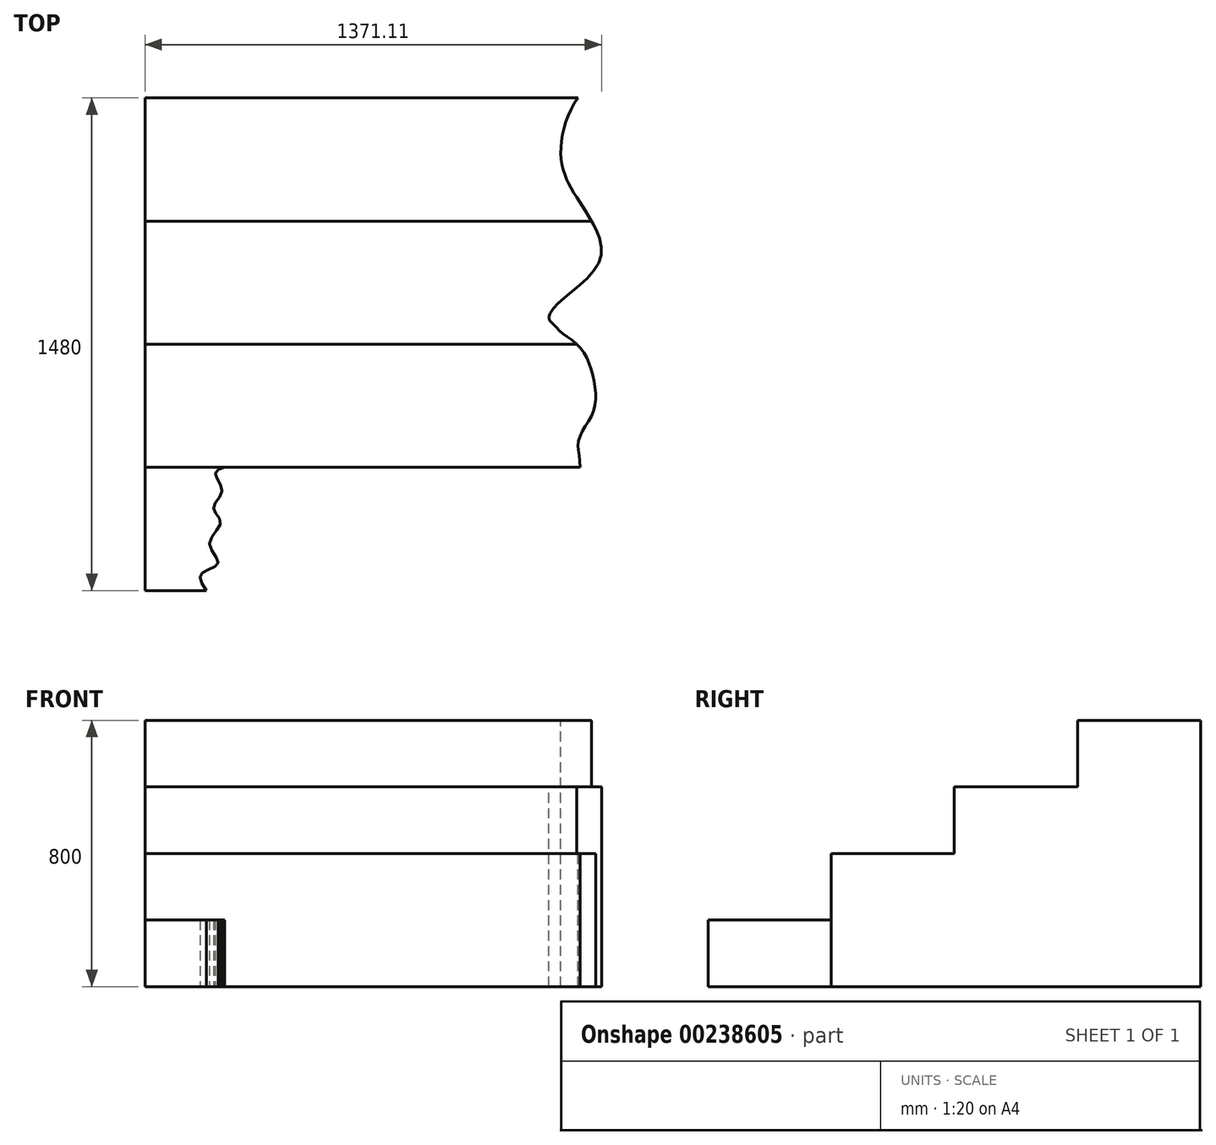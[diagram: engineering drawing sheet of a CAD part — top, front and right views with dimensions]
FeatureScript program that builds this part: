
annotation { "Feature Type Name" : "Feature", "Feature Type Description" : "" }
export const myFeature = defineFeature(function(context is Context, id is Id, definition is map)
    precondition{}
    {
        {
            var Q0;
            Q0=qCreatedBy(makeId("Right.planeOp"),FACE);
            var sketch = newSketch(context, id + "F0", { "sketchPlane" : qUnion([Q0])});
            skLineSegment(sketch, "E0.bottom", {"start": v(0, 0) * mm, "end": v(-370, 0) * mm});
            skLineSegment(sketch, "E0.top", {"start": v(0, 200) * mm, "end": v(-370, 200) * mm});
            skLineSegment(sketch, "E0.left", {"start": v(0, 0) * mm, "end": v(0, 200) * mm});
            skLineSegment(sketch, "E0.right", {"start": v(-370, 0) * mm, "end": v(-370, 200) * mm});
            skSolve(sketch);
        }
        {
            var Q0;
            Q0=makeQuery(id+"F0.imprint","IMPRINT",FACE,{"disambiguationData":[TD([[makeQuery(id+"F0.imprint","IMPRINT",EDGE,{"derivedFrom":sQuery(id+"F0.wireOp",EDGE,"E0.bottom")}),-1.0]])]});
            extrude(context, id + "F1", {"entities" : qUnion([Q0]), "depth" : 250 * mm});
        }
        {
            var Q0;
            Q0=qCreatedBy(makeId("Right.planeOp"),FACE);
            var sketch = newSketch(context, id + "F2", { "sketchPlane" : qUnion([Q0])});
            skLineSegment(sketch, "E1", {"start": v(0, 0) * mm, "end": v(0, 400) * mm});
            skLineSegment(sketch, "E2", {"start": v(0, 400) * mm, "end": v(370, 400) * mm});
            skLineSegment(sketch, "E3", {"start": v(370, 400) * mm, "end": v(370, 600) * mm});
            skLineSegment(sketch, "E4", {"start": v(370, 600) * mm, "end": v(740, 600) * mm});
            skLineSegment(sketch, "E5", {"start": v(740, 600) * mm, "end": v(740, 800) * mm});
            skLineSegment(sketch, "E6", {"start": v(740, 800) * mm, "end": v(1110, 800) * mm});
            skLineSegment(sketch, "E7", {"start": v(1110, 800) * mm, "end": v(1110, 0) * mm});
            skLineSegment(sketch, "E8", {"start": v(1110, 0) * mm, "end": v(0, 0) * mm});
            skSolve(sketch);
        }
        {
            var Q0;
            Q0 = qSketchRegion(id + "F2", true);
            extrude(context, id + "F3", {"entities" : qUnion([Q0]), "operationType" : NewBodyOperationType.ADD, "depth" : 1400 * mm});
        }
        {
            var Q0;
            Q0=makeQuery(id+"F1.opExtrude","SWEPT_FACE",FACE,{"disambiguationData":[OSD([sQuery(id+"F0.wireOp",EDGE,"E0.top")])]});
            var sketch = newSketch(context, id + "F4", { "sketchPlane" : qUnion([Q0])});
            skFitSpline(sketch, "E9", {"points": [v(250, 0) * mm, v(210.88, -17.8) * mm, v(230.52, -70.84) * mm, v(204.98, -121.92) * mm, v(226.6, -165.15) * mm, v(193.2, -229.98) * mm, v(218.73, -288.92) * mm, v(169.62, -318.4) * mm, v(183.37, -370) * mm, v(250, -434.31) * mm, v(289.46, -340) * mm, v(338.58, -241.77) * mm, v(316.97, -153.36) * mm, v(313.04, -127.82) * mm, v(301.25, -43.33) * mm, v(250, 0) * mm]});
            skSolve(sketch);
        }
        {
            var Q0;
            {var subQ1=sQuery(id+"F0.wireOp",EDGE,"E0.top");var subQ6=makeQuery(id+"F1.opExtrude","CAP_EDGE",EDGE,{"disambiguationData":[OSD([subQ1])],"isStart":false});Q0=makeQuery(id+"F4.imprint","IMPRINT",FACE,{"disambiguationData":[TD([[makeQuery(id+"F4.imprint","IMPRINT",EDGE,{"derivedFrom":subQ6}),-1.0]])]});}
            extrude(context, id + "F5", {"entities" : qUnion([Q0]), "operationType" : NewBodyOperationType.REMOVE, "endBound" : BoundingType.THROUGH_ALL, "oppositeDirection" : true, "depth" : 25 * mm});
        }
        {
            var Q0;
            Q0=qCreatedBy(makeId("Top.planeOp"),FACE);
            var sketch = newSketch(context, id + "F6", { "sketchPlane" : qUnion([Q0])});
            skFitSpline(sketch, "E10", {"points": [v(1355.04, 1158.75) * mm, v(1248.78, 943.7) * mm, v(1312.03, 786.84) * mm, v(1367.7, 627.45) * mm, v(1241.2, 493.36) * mm, v(1213.36, 445.28) * mm, v(1228.54, 427.57) * mm, v(1251.31, 404.8) * mm, v(1306.97, 359.26) * mm, v(1347.45, 265.65) * mm, v(1344.92, 164.45) * mm, v(1301.91, 80.96) * mm, v(1306.97, 0) * mm, v(1312.03, -121.44) * mm, v(1506.85, 0) * mm, v(1618.17, 1024.66) * mm, v(1355.04, 1158.75) * mm]});
            skSolve(sketch);
        }
        {
            var Q0;
            Q0=makeQuery(id+"F6.imprint","IMPRINT",FACE,{"disambiguationData":[TD([[makeQuery(id+"F6.imprint","IMPRINT",EDGE,{"derivedFrom":sQuery(id+"F6.wireOp",EDGE,"E10")}),1.0]])]});
            extrude(context, id + "F7", {"entities" : qUnion([Q0]), "operationType" : NewBodyOperationType.REMOVE, "endBound" : BoundingType.THROUGH_ALL, "depth" : 25 * mm});
        }
    });
